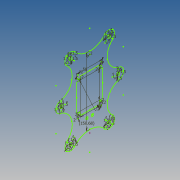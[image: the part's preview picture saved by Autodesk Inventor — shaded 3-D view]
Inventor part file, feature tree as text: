
AUTODESK INVENTOR PART (.ipt)
format: ipt  version: 2014 (Build 180170000, 170)  size: 140,288 bytes
history: native  units: mm
features: sketch x2
ambient origin geometry x8: Origin, YZ Plane, XZ Plane, XY Plane, X Axis, Y Axis, Z Axis, Center Point
feature tree (2):
  sketch  "Sketch1"  dims[d1=60.0mm]
  sketch  "Sketch2"  dims[d2=25.0mm d3=2.0mm d4=2.0mm d5=25.0mm d6=7.0mm d7=25.0mm d8=7.0mm d9=150.680282mm d10=25.0mm d11=7.0mm d12=1.5mm d13=1.5mm d14=1.5mm d15=1.5mm d16=2.0mm d17=1.5mm d18=1.5mm d19=1.5mm d20=1.5mm d21=1.5mm d22=1.5mm d23=1.5mm d24=1.5mm d25=1.5mm d26=1.5mm d27=1.5mm d28=1.5mm d29=1.5mm d30=1.5mm d31=1.5mm d32=1.5mm d33=25.0mm d34=25.0mm d35=7.0mm d36=7.0mm d37=1.5mm d38=1.5mm d39=1.5mm d40=1.5mm d41=2.0mm d42=2.0mm d43=2.0mm d44=2.0mm d45=2.0mm d46=8.0mm d47=2.0mm d48=8.0mm d49=2.0mm d50=8.0mm d51=42.0mm d52=60.0mm d53=42.0mm d54=58.0mm d55=60.0mm d56=42.0mm d57=7.0mm]
